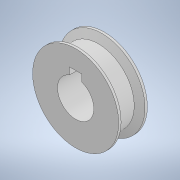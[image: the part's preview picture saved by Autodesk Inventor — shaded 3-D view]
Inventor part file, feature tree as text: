
AUTODESK INVENTOR PART (.ipt)
format: ipt  version: 2022 (Build 260153000, 153)  size: 139,776 bytes
history: native  units: mm
features: sketch x2, extrude x1, revolve x1, thicken_offset x1, projected_geometry x1
ambient origin geometry x8: Origin, YZ Plane, XZ Plane, XY Plane, X Axis, Y Axis, Z Axis, Center Point
bodies: Body1 (feature_tree)
feature tree (6):
  extrude  "Extrusion3"  Depth=15.0mm
  sketch  "Sketch5"  dims[d19=5.0mm d20=30.0mm d21=12.0mm d22=0.0mm d23=7.0mm d24=3.0mm d25=1.0mm d26=1.0mm d28=90.0deg d29=0.1mm d30=0.1mm]
  revolve  "Revolution1"  [1 undecoded]
  thicken_offset  "Thicken1"
  sketch  "Sketch4"  dims[d17=15.0mm d18=5.0mm]
  projected_geometry  "Projected Loop3"
note: 1 required parameter value undecoded (feature->parameter linkage not recoverable at this tier; creation-order binding heuristic only, values carry confidence <= 0.55)
